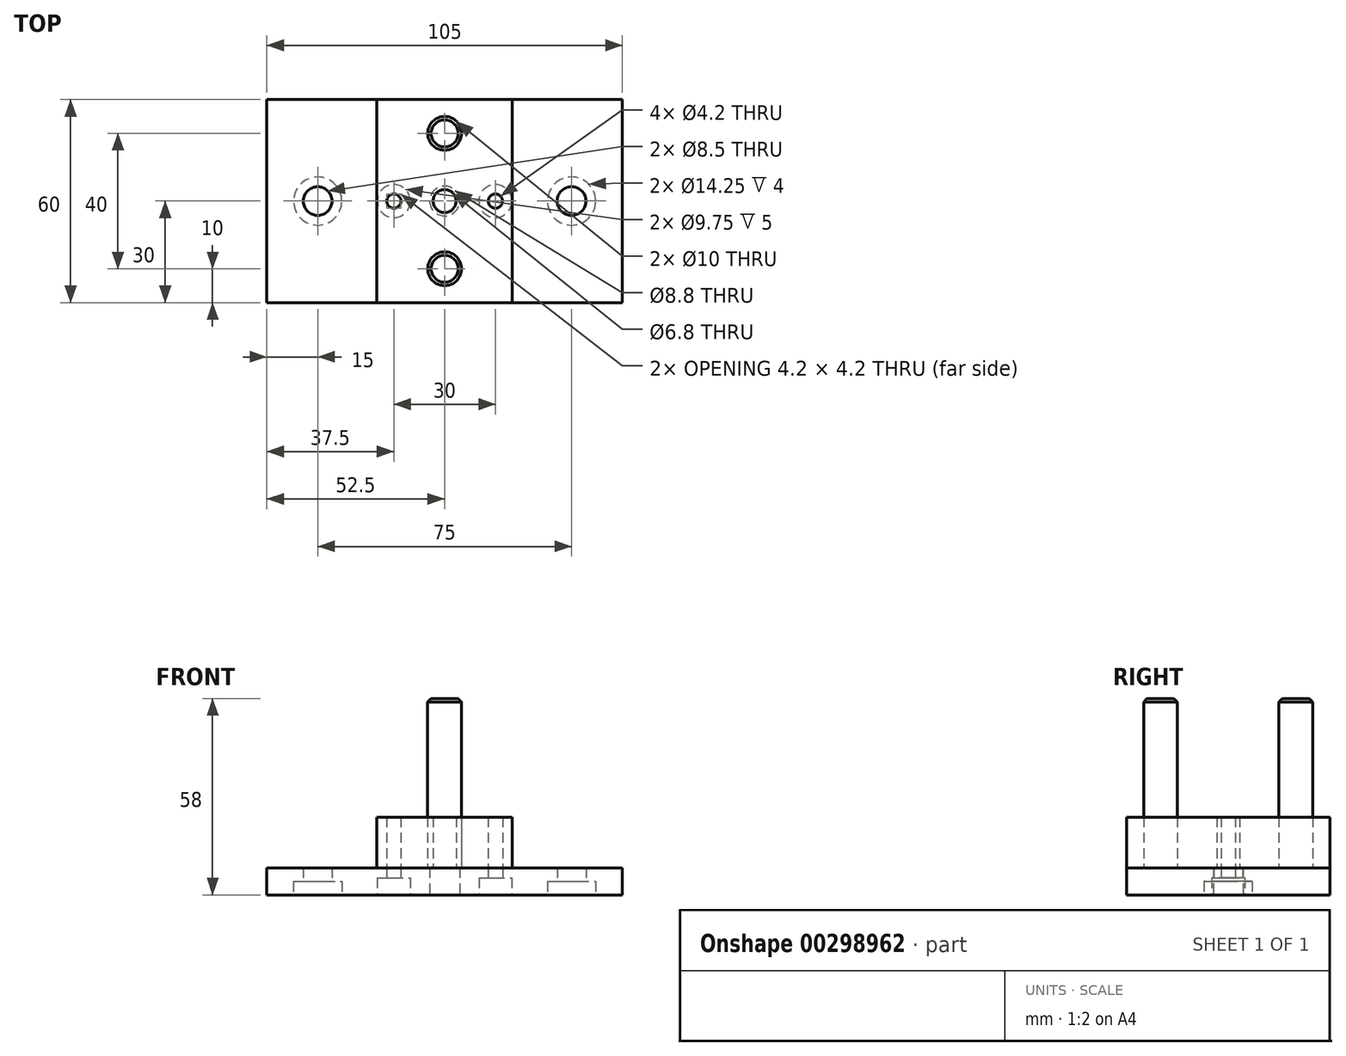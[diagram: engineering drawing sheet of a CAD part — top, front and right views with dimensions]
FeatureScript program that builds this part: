
annotation { "Feature Type Name" : "Feature", "Feature Type Description" : "" }
export const myFeature = defineFeature(function(context is Context, id is Id, definition is map)
    precondition{}
    {
        {
            var Q0;
            Q0=qCreatedBy(makeId("Top.planeOp"),FACE);
            var sketch = newSketch(context, id + "F0", { "sketchPlane" : qUnion([Q0])});
            skLineSegment(sketch, "E0.bottom", {"start": v(52.5, 30) * mm, "end": v(-52.5, 30) * mm});
            skLineSegment(sketch, "E0.top", {"start": v(52.5, -30) * mm, "end": v(-52.5, -30) * mm});
            skLineSegment(sketch, "E0.left", {"start": v(52.5, 30) * mm, "end": v(52.5, -30) * mm});
            skLineSegment(sketch, "E0.right", {"start": v(-52.5, 30) * mm, "end": v(-52.5, -30) * mm});
            skPoint(sketch, "E0.middle", {"position": v(0, 0) * mm});
            skPoint(sketch, "E1", {"position": v(-37.5, 0) * mm});
            skPoint(sketch, "E2", {"position": v(-15, 0) * mm});
            skPoint(sketch, "E3.MirrorP", {"position": v(15, 0) * mm});
            skPoint(sketch, "E4.MirrorP", {"position": v(37.5, 0) * mm});
            skSolve(sketch);
        }
        {
            var Q0;
            Q0 = qSketchRegion(id + "F0", true);
            extrude(context, id + "F1", {"entities" : qUnion([Q0]), "depth" : 8 * mm});
        }
        {
            var Q0;
            Q0=sQuery(id+"F0.wireOp",VERTEX,"E1");
            var Q1;
            Q1=sQuery(id+"F0.wireOp",VERTEX,"E4.MirrorP");
            var Q2;
            Q2=makeQuery(id+"F1.opExtrude","SWEPT_BODY",BODY,{"disambiguationData":[OSD([sQuery(id+"F0.wireOp",EDGE,"E0.bottom"),sQuery(id+"F0.wireOp",EDGE,"E0.top"),sQuery(id+"F0.wireOp",EDGE,"E0.left"),sQuery(id+"F0.wireOp",EDGE,"E0.right")])]});
            hole(context, id + "F2", {"style" : HoleStyle.C_BORE, "endStyle" : HoleEndStyle.THROUGH, "oppositeDirection" : true, "holeDiameter" : 8.5 * mm, "cBoreDiameter" : 14.25 * mm, "cBoreDepth" : 4 * mm, "isTappedThrough" : true, "tappedDepth" : 12 * mm, "tapClearance" : 3, "locations" : qUnion([Q0, Q1]), "scope" : qUnion([Q2])});
        }
        {
            var Q0;
            Q0=sQuery(id+"F0.wireOp",VERTEX,"E0.middle");
            var Q1;
            Q1=makeQuery(id+"F1.opExtrude","SWEPT_BODY",BODY,{"disambiguationData":[OSD([sQuery(id+"F0.wireOp",EDGE,"E0.bottom"),sQuery(id+"F0.wireOp",EDGE,"E0.top"),sQuery(id+"F0.wireOp",EDGE,"E0.left"),sQuery(id+"F0.wireOp",EDGE,"E0.right")])]});
            hole(context, id + "F3", {"style" : HoleStyle.SIMPLE, "endStyle" : HoleEndStyle.THROUGH, "oppositeDirection" : true, "standardTappedOrClearance" : lookupTablePath({ "standard" : "ISO", "fit" : "Normal", "size" : "M8", "type" : "Clearance" }), "standardBlindInLast" : lookupTablePath({ "fit" : "Standard", "standard" : "ISO", "size" : "M8", "type" : "Clearance" }), "holeDiameter" : 8.8 * mm, "isTappedThrough" : true, "tappedDepth" : 12 * mm, "tapClearance" : 3, "locations" : qUnion([Q0]), "scope" : qUnion([Q1])});
        }
        {
            var Q0;
            Q0=sQuery(id+"F0.wireOp",VERTEX,"E2");
            var Q1;
            Q1=sQuery(id+"F0.wireOp",VERTEX,"E3.MirrorP");
            var Q2;
            Q2=makeQuery(id+"F1.opExtrude","SWEPT_BODY",BODY,{"disambiguationData":[OSD([sQuery(id+"F0.wireOp",EDGE,"E0.bottom"),sQuery(id+"F0.wireOp",EDGE,"E0.top"),sQuery(id+"F0.wireOp",EDGE,"E0.left"),sQuery(id+"F0.wireOp",EDGE,"E0.right")])]});
            hole(context, id + "F4", {"style" : HoleStyle.C_BORE, "endStyle" : HoleEndStyle.THROUGH, "oppositeDirection" : true, "standardTappedOrClearance" : lookupTablePath({ "standard" : "ISO", "engagement" : "75%", "pitch" : "0.8 mm", "size" : "M5", "type" : "Tapped" }), "standardBlindInLast" : lookupTablePath({ "standard" : "ISO", "engagement" : "75%", "pitch" : "0.8 mm", "size" : "M5", "type" : "Tapped" }), "holeDiameter" : 4.2 * mm, "cBoreDiameter" : 9.75 * mm, "cBoreDepth" : 5 * mm, "showTappedDepth" : true, "isTappedThrough" : true, "tappedDepth" : 12 * mm, "tapClearance" : 3, "locations" : qUnion([Q0, Q1]), "scope" : qUnion([Q2]), "majorDiameter" : 5 * mm});
        }
        {
            var Q0;
            Q0=makeQuery(id+"F1.opExtrude","CAP_FACE",FACE,{"disambiguationData":[OSD([sQuery(id+"F0.wireOp",EDGE,"E0.bottom"),sQuery(id+"F0.wireOp",EDGE,"E0.top"),sQuery(id+"F0.wireOp",EDGE,"E0.left"),sQuery(id+"F0.wireOp",EDGE,"E0.right")])],"isStart":false});
            var sketch = newSketch(context, id + "F5", { "sketchPlane" : qUnion([Q0])});
            skLineSegment(sketch, "E5.bottom", {"start": v(20, 30) * mm, "end": v(-20, 30) * mm});
            skLineSegment(sketch, "E5.top", {"start": v(20, -30) * mm, "end": v(-20, -30) * mm});
            skLineSegment(sketch, "E5.left", {"start": v(20, 30) * mm, "end": v(20, -30) * mm});
            skLineSegment(sketch, "E5.right", {"start": v(-20, 30) * mm, "end": v(-20, -30) * mm});
            skPoint(sketch, "E5.middle", {"position": v(0, 0) * mm});
            skPoint(sketch, "E6", {"position": v(0, 20) * mm});
            skPoint(sketch, "E7", {"position": v(-15, 0) * mm});
            skPoint(sketch, "E8.MirrorP", {"position": v(0, -20) * mm});
            skPoint(sketch, "E9.MirrorP", {"position": v(15, 0) * mm});
            skSolve(sketch);
        }
        {
            var Q0;
            Q0 = qSketchRegion(id + "F5", true);
            extrude(context, id + "F6", {"entities" : qUnion([Q0]), "depth" : 15 * mm});
        }
        {
            var Q0;
            Q0=sQuery(id+"F5.wireOp",VERTEX,"E6");
            var Q1;
            Q1=sQuery(id+"F5.wireOp",VERTEX,"E8.MirrorP");
            var Q2;
            Q2=makeQuery(id+"F6.opExtrude","SWEPT_BODY",BODY,{"disambiguationData":[OSD([sQuery(id+"F5.wireOp",EDGE,"E5.bottom"),sQuery(id+"F5.wireOp",EDGE,"E5.top"),sQuery(id+"F5.wireOp",EDGE,"E5.left"),sQuery(id+"F5.wireOp",EDGE,"E5.right")])]});
            hole(context, id + "F7", {"style" : HoleStyle.SIMPLE, "endStyle" : HoleEndStyle.THROUGH, "oppositeDirection" : true, "holeDiameter" : 10 * mm, "isTappedThrough" : true, "tappedDepth" : 12 * mm, "tapClearance" : 3, "locations" : qUnion([Q0, Q1]), "scope" : qUnion([Q2])});
        }
        {
            var Q0;
            Q0=sQuery(id+"F5.wireOp",VERTEX,"E7");
            var Q1;
            Q1=sQuery(id+"F5.wireOp",VERTEX,"E9.MirrorP");
            var Q2;
            Q2=makeQuery(id+"F6.opExtrude","SWEPT_BODY",BODY,{"disambiguationData":[OSD([sQuery(id+"F5.wireOp",EDGE,"E5.bottom"),sQuery(id+"F5.wireOp",EDGE,"E5.top"),sQuery(id+"F5.wireOp",EDGE,"E5.left"),sQuery(id+"F5.wireOp",EDGE,"E5.right")])]});
            hole(context, id + "F8", {"style" : HoleStyle.SIMPLE, "endStyle" : HoleEndStyle.THROUGH, "oppositeDirection" : true, "standardTappedOrClearance" : lookupTablePath({ "standard" : "ISO", "engagement" : "75%", "pitch" : "0.8 mm", "size" : "M5", "type" : "Tapped" }), "standardBlindInLast" : lookupTablePath({ "standard" : "ISO", "engagement" : "75%", "pitch" : "0.8 mm", "size" : "M5", "type" : "Tapped" }), "holeDiameter" : 4.2 * mm, "showTappedDepth" : true, "isTappedThrough" : true, "tappedDepth" : 12 * mm, "tapClearance" : 3, "locations" : qUnion([Q0, Q1]), "scope" : qUnion([Q2]), "majorDiameter" : 5 * mm});
        }
        {
            var Q0;
            Q0=sQuery(id+"F5.wireOp",VERTEX,"E5.middle");
            var Q1;
            Q1=makeQuery(id+"F6.opExtrude","SWEPT_BODY",BODY,{"disambiguationData":[OSD([sQuery(id+"F5.wireOp",EDGE,"E5.bottom"),sQuery(id+"F5.wireOp",EDGE,"E5.top"),sQuery(id+"F5.wireOp",EDGE,"E5.left"),sQuery(id+"F5.wireOp",EDGE,"E5.right")])]});
            hole(context, id + "F9", {"style" : HoleStyle.SIMPLE, "endStyle" : HoleEndStyle.THROUGH, "oppositeDirection" : true, "standardTappedOrClearance" : lookupTablePath({ "standard" : "ISO", "engagement" : "75%", "pitch" : "1.25 mm", "size" : "M8", "type" : "Tapped" }), "standardBlindInLast" : lookupTablePath({ "standard" : "ISO", "engagement" : "75%", "pitch" : "1.25 mm", "size" : "M8", "type" : "Tapped" }), "holeDiameter" : 6.8 * mm, "showTappedDepth" : true, "isTappedThrough" : true, "tappedDepth" : 12 * mm, "tapClearance" : 3, "locations" : qUnion([Q0]), "scope" : qUnion([Q1]), "majorDiameter" : 8 * mm});
        }
        {
            var Q0;
            {var subQ4=sQuery(id+"F5.wireOp",EDGE,"E5.right");Q0=makeQuery(id+"F5.imprint","IMPRINT",FACE,{"disambiguationData":[TD([[makeQuery(id+"F5.imprint","IMPRINT",EDGE,{"derivedFrom":subQ4}),-1.0]])]});}
            var sketch = newSketch(context, id + "F10", { "sketchPlane" : qUnion([Q0])});
            skCircle(sketch, "E10", {"center": v(0, -20) * mm, "radius": 5 * mm});
            skCircle(sketch, "E11.MirrorC", {"center": v(0, 20) * mm, "radius": 5 * mm});
            skSolve(sketch);
        }
        {
            var Q0;
            Q0 = qSketchRegion(id + "F10", true);
            extrude(context, id + "F11", {"entities" : qUnion([Q0]), "depth" : 50 * mm});
        }
        {
            var Q0;
            Q0=makeQuery(id+"F11.opExtrude","CAP_EDGE",EDGE,{"disambiguationData":[OSD([sQuery(id+"F10.wireOp",EDGE,"E10")])],"isStart":false});
            var Q1;
            Q1=makeQuery(id+"F11.opExtrude","CAP_EDGE",EDGE,{"disambiguationData":[OSD([sQuery(id+"F10.wireOp",EDGE,"E11.MirrorC")])],"isStart":false});
            chamfer(context, id + "F12", {"entities" : qUnion([Q0, Q1]), "width" : 1 * mm, "tangentPropagation" : true});
        }
    });
